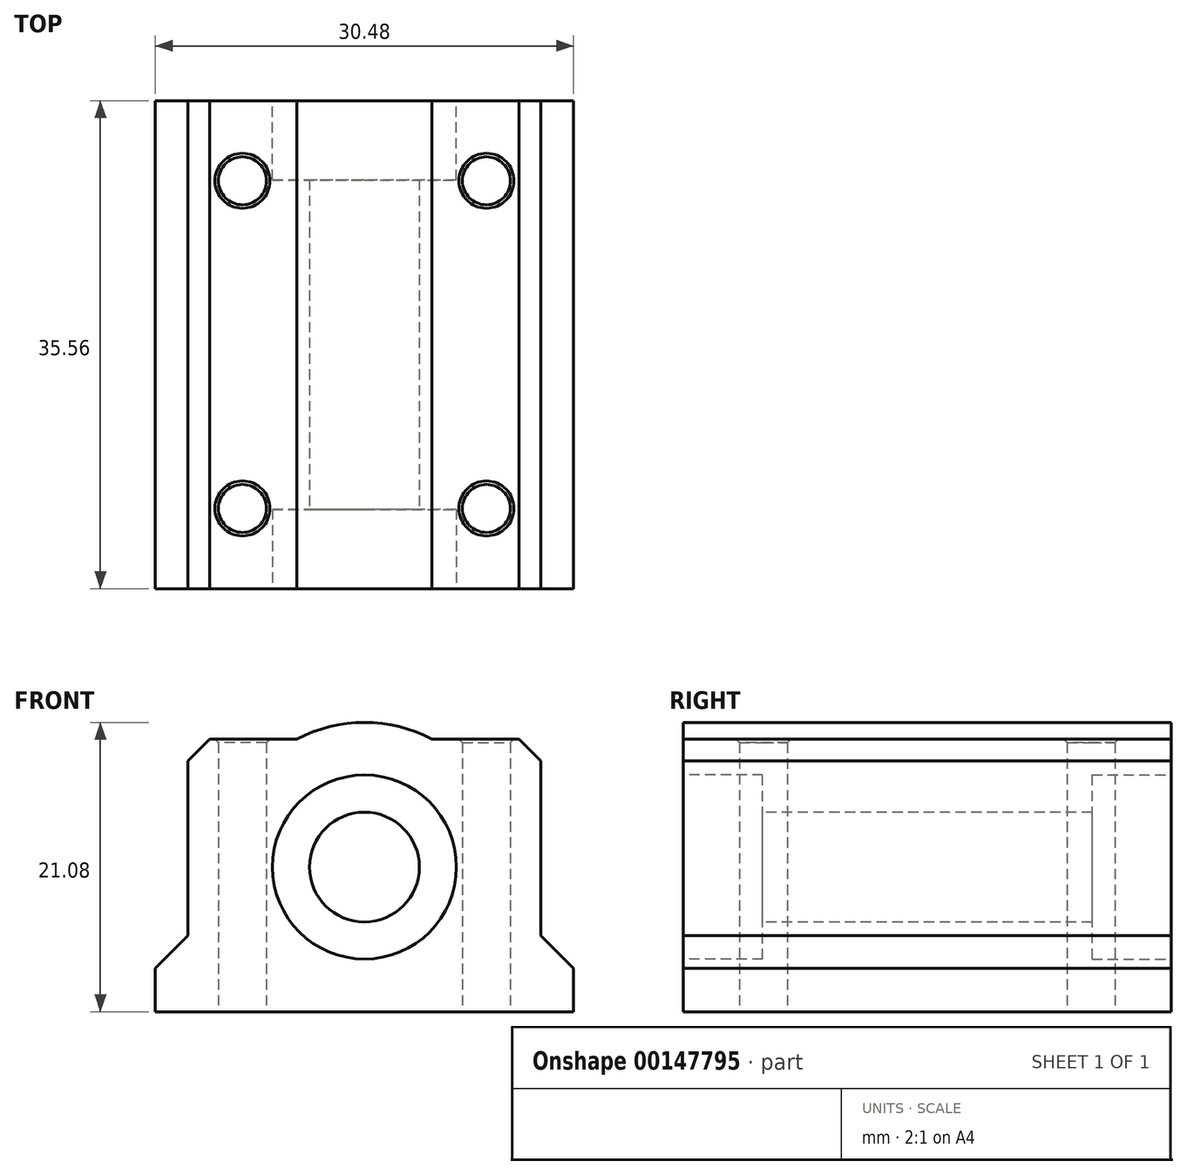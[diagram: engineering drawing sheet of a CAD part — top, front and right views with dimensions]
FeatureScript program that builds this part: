
annotation { "Feature Type Name" : "Feature", "Feature Type Description" : "" }
export const myFeature = defineFeature(function(context is Context, id is Id, definition is map)
    precondition{}
    {
        {
            var Q0;
            Q0=qCreatedBy(makeId("Top.planeOp"),FACE);
            var sketch = newSketch(context, id + "F0", { "sketchPlane" : qUnion([Q0])});
            skLineSegment(sketch, "E0.bottom", {"start": v(0, 0) * mm, "end": v(30.48, 0) * mm});
            skLineSegment(sketch, "E0.top", {"start": v(0, -35.56) * mm, "end": v(30.48, -35.56) * mm});
            skLineSegment(sketch, "E0.left", {"start": v(0, 0) * mm, "end": v(0, -35.56) * mm});
            skLineSegment(sketch, "E0.right", {"start": v(30.48, 0) * mm, "end": v(30.48, -35.56) * mm});
            skLineSegment(sketch, "E1", {"start": v(15.24, 0) * mm, "end": v(15.24, -35.56) * mm, "construction": true});
            skLineSegment(sketch, "E2.bottom", {"start": v(6.35, -5.84) * mm, "end": v(24.13, -5.84) * mm, "construction": true});
            skLineSegment(sketch, "E2.top", {"start": v(6.35, -29.72) * mm, "end": v(24.13, -29.72) * mm, "construction": true});
            skLineSegment(sketch, "E2.left", {"start": v(6.35, -5.84) * mm, "end": v(6.35, -29.72) * mm, "construction": true});
            skLineSegment(sketch, "E2.right", {"start": v(24.13, -5.84) * mm, "end": v(24.13, -29.72) * mm, "construction": true});
            skPoint(sketch, "E2.middle", {"position": v(15.24, -17.78) * mm});
            skCircle(sketch, "E3", {"center": v(6.35, -5.84) * mm, "radius": 1.75 * mm});
            skCircle(sketch, "E4", {"center": v(24.13, -5.84) * mm, "radius": 1.75 * mm});
            skCircle(sketch, "E5", {"center": v(24.13, -29.72) * mm, "radius": 1.75 * mm});
            skCircle(sketch, "E6", {"center": v(6.35, -29.72) * mm, "radius": 1.75 * mm});
            skSolve(sketch);
        }
        {
            var Q0;
            Q0=qSketchRegion(id+"F0",true);
            extrude(context, id + "F1", {"entities" : qUnion([Q0]), "depth" : 21.08 * mm});
        }
        {
            var Q0;
            Q0=makeQuery(id+"F1.opExtrude","SWEPT_FACE",FACE,{"disambiguationData":[OSD([sQuery(id+"F0.wireOp",EDGE,"E0.top")])]});
            var sketch = newSketch(context, id + "F2", { "sketchPlane" : qUnion([Q0])});
            skLineSegment(sketch, "E7", {"start": v(15.24, 21.08) * mm, "end": v(15.24, 0) * mm, "construction": true});
            skCircle(sketch, "E8", {"center": v(15.24, 10.54) * mm, "radius": 4 * mm});
            skArc(sketch, "E9", {"start": v(20.16, 19.86) * mm, "mid": v(15.24, 21.08) * mm, "end": v(10.32, 19.86) * mm});
            skLineSegment(sketch, "E10", {"start": v(24.13, 21.08) * mm, "end": v(24.13, 19.86) * mm, "construction": true});
            skLineSegment(sketch, "E11", {"start": v(20.16, 19.86) * mm, "end": v(28.1, 19.86) * mm});
            skLineSegment(sketch, "E12", {"start": v(28.1, 19.86) * mm, "end": v(28.1, 5.56) * mm});
            skLineSegment(sketch, "E13", {"start": v(28.1, 5.56) * mm, "end": v(30.48, 3.18) * mm});
            skLineSegment(sketch, "E14", {"start": v(30.48, 3.18) * mm, "end": v(30.48, 21.08) * mm});
            skLineSegment(sketch, "E15", {"start": v(30.48, 21.08) * mm, "end": v(15.24, 21.08) * mm});
            skLineSegment(sketch, "E16", {"start": v(10.32, 19.86) * mm, "end": v(2.38, 19.86) * mm});
            skLineSegment(sketch, "E17", {"start": v(2.38, 19.86) * mm, "end": v(2.38, 5.56) * mm});
            skLineSegment(sketch, "E18", {"start": v(2.38, 5.56) * mm, "end": v(0, 3.17) * mm});
            skLineSegment(sketch, "E19", {"start": v(15.24, 21.08) * mm, "end": v(0, 21.08) * mm});
            skLineSegment(sketch, "E20", {"start": v(0, 21.08) * mm, "end": v(0, 3.17) * mm});
            skSolve(sketch);
        }
        {
            var Q0;
            Q0=qSketchRegion(id+"F2",true);
            var Q1;
            Q1=makeQuery(id+"F1.opExtrude","SWEPT_FACE",FACE,{"disambiguationData":[OSD([sQuery(id+"F0.wireOp",EDGE,"E0.bottom")])]});
            extrude(context, id + "F3", {"entities" : qUnion([Q0]), "operationType" : NewBodyOperationType.REMOVE, "endBound" : BoundingType.UP_TO_SURFACE, "oppositeDirection" : true, "endBoundEntityFace" : qUnion([Q1]), "depth" : 25.4 * mm});
        }
        {
            var Q0;
            Q0=makeQuery(id+"F3.boolean.opBoolean","COPY",EDGE,{"derivedFrom":makeQuery(id+"F3.opExtrude","SWEPT_EDGE",EDGE,{"disambiguationData":[OSD([sQuery(id+"F2.wireOp",EDGE,"E11"),sQuery(id+"F2.wireOp",EDGE,"E12")])]})});
            var Q1;
            Q1=makeQuery(id+"F3.boolean.opBoolean","COPY",EDGE,{"derivedFrom":makeQuery(id+"F3.opExtrude","SWEPT_EDGE",EDGE,{"disambiguationData":[OSD([sQuery(id+"F2.wireOp",EDGE,"E16"),sQuery(id+"F2.wireOp",EDGE,"E17")])]})});
            chamfer(context, id + "F4", {"entities" : qUnion([Q0, Q1]), "width" : 1.59 * mm, "tangentPropagation" : true});
        }
        {
            var Q0;
            Q0=makeQuery(id+"F3.boolean.opBoolean","INTERSECT",EDGE,{"derivedFrom":[makeQuery(id+"F1.opExtrude","SWEPT_FACE",FACE,{"disambiguationData":[OSD([sQuery(id+"F0.wireOp",EDGE,"E5")])]}),makeQuery(id+"F3.opExtrude","SWEPT_FACE",FACE,{"disambiguationData":[OSD([sQuery(id+"F2.wireOp",EDGE,"E11")])]})]});
            var Q1;
            Q1=makeQuery(id+"F3.boolean.opBoolean","INTERSECT",EDGE,{"derivedFrom":[makeQuery(id+"F1.opExtrude","SWEPT_FACE",FACE,{"disambiguationData":[OSD([sQuery(id+"F0.wireOp",EDGE,"E4")])]}),makeQuery(id+"F3.opExtrude","SWEPT_FACE",FACE,{"disambiguationData":[OSD([sQuery(id+"F2.wireOp",EDGE,"E11")])]})]});
            var Q2;
            Q2=makeQuery(id+"F3.boolean.opBoolean","INTERSECT",EDGE,{"derivedFrom":[makeQuery(id+"F1.opExtrude","SWEPT_FACE",FACE,{"disambiguationData":[OSD([sQuery(id+"F0.wireOp",EDGE,"E3")])]}),makeQuery(id+"F3.opExtrude","SWEPT_FACE",FACE,{"disambiguationData":[OSD([sQuery(id+"F2.wireOp",EDGE,"E16")])]})]});
            var Q3;
            Q3=makeQuery(id+"F3.boolean.opBoolean","INTERSECT",EDGE,{"derivedFrom":[makeQuery(id+"F1.opExtrude","SWEPT_FACE",FACE,{"disambiguationData":[OSD([sQuery(id+"F0.wireOp",EDGE,"E6")])]}),makeQuery(id+"F3.opExtrude","SWEPT_FACE",FACE,{"disambiguationData":[OSD([sQuery(id+"F2.wireOp",EDGE,"E16")])]})]});
            chamfer(context, id + "F5", {"entities" : qUnion([Q0, Q1, Q2, Q3]), "width" : 0.25 * mm, "tangentPropagation" : true});
        }
        {
            var Q0;
            Q0=makeQuery(id+"F1.opExtrude","SWEPT_FACE",FACE,{"disambiguationData":[OSD([sQuery(id+"F0.wireOp",EDGE,"E0.top")])]});
            var sketch = newSketch(context, id + "F6", { "sketchPlane" : qUnion([Q0])});
            skCircle(sketch, "E21", {"center": v(15.24, 10.54) * mm, "radius": 6.7 * mm});
            skSolve(sketch);
        }
        {
            var Q0;
            Q0=qSketchRegion(id+"F6",true);
            extrude(context, id + "F7", {"entities" : qUnion([Q0]), "operationType" : NewBodyOperationType.REMOVE, "oppositeDirection" : true, "depth" : 5.78 * mm});
        }
        {
            var Q0;
            Q0=makeQuery(id+"F1.opExtrude","SWEPT_FACE",FACE,{"disambiguationData":[OSD([sQuery(id+"F0.wireOp",EDGE,"E0.bottom")])]});
            var sketch = newSketch(context, id + "F8", { "sketchPlane" : qUnion([Q0])});
            skCircle(sketch, "E22", {"center": v(-15.24, 10.54) * mm, "radius": 6.7 * mm});
            skSolve(sketch);
        }
        {
            var Q0;
            Q0=qSketchRegion(id+"F8",true);
            extrude(context, id + "F9", {"entities" : qUnion([Q0]), "operationType" : NewBodyOperationType.REMOVE, "oppositeDirection" : true, "depth" : 5.78 * mm});
        }
    });
